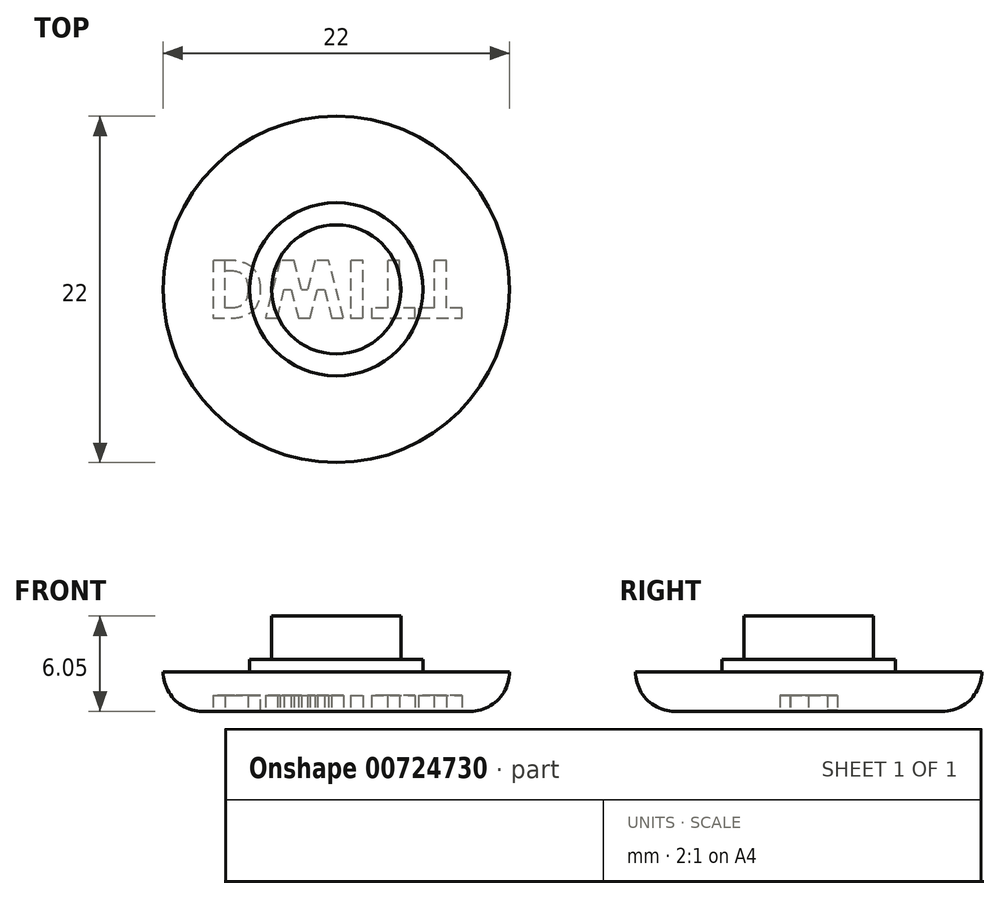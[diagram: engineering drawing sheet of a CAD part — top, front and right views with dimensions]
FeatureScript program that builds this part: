
annotation { "Feature Type Name" : "Feature", "Feature Type Description" : "" }
export const myFeature = defineFeature(function(context is Context, id is Id, definition is map)
    precondition{}
    {
        {
            var Q0;
            Q0=qCreatedBy(makeId("Top.planeOp"),FACE);
            var sketch = newSketch(context, id + "F0", { "sketchPlane" : qUnion([Q0])});
            skCircle(sketch, "E0", {"center": v(0, 0) * mm, "radius": 11 * mm});
            skCircle(sketch, "E1", {"center": v(0, 0) * mm, "radius": 4.1 * mm});
            skCircle(sketch, "E2", {"center": v(0, 0) * mm, "radius": 5.5 * mm});
            skSolve(sketch);
        }
        {
            var Q0;
            Q0=makeQuery(id+"F0.imprint","IMPRINT",FACE,{"disambiguationData":[TD([[makeQuery(id+"F0.imprint","IMPRINT",EDGE,{"derivedFrom":sQuery(id+"F0.wireOp",EDGE,"E0")}),1.0]])]});
            extrude(context, id + "F1", {"entities" : qUnion([Q0]), "depth" : 2.5 * mm, "offsetDistance" : 25 * mm});
        }
        {
            var Q0;
            Q0=makeQuery(id+"F0.imprint","IMPRINT",FACE,{"disambiguationData":[TD([[makeQuery(id+"F0.imprint","IMPRINT",EDGE,{"derivedFrom":sQuery(id+"F0.wireOp",EDGE,"E1")}),-1.0]])]});
            var Q1;
            Q1=makeQuery(id+"F1.opExtrude","CAP_FACE",FACE,{"disambiguationData":[OSD([sQuery(id+"F0.wireOp",EDGE,"E0"),sQuery(id+"F0.wireOp",EDGE,"E2")])],"isStart":false});
            extrude(context, id + "F2", {"entities" : qUnion([Q0]), "operationType" : NewBodyOperationType.ADD, "endBound" : BoundingType.UP_TO_SURFACE, "depth" : 25 * mm, "endBoundEntityFace" : qUnion([Q1]), "hasOffset" : true, "offsetDistance" : .8 * mm, "offsetOppositeDirection" : true});
        }
        {
            var Q0;
            Q0=makeQuery(id+"F0.imprint","IMPRINT",FACE,{"disambiguationData":[TD([[makeQuery(id+"F0.imprint","IMPRINT",EDGE,{"derivedFrom":sQuery(id+"F0.wireOp",EDGE,"E1")}),1.0]])]});
            var Q1;
            Q1=makeQuery(id+"F2.opExtrude","CAP_FACE",FACE,{"disambiguationData":[OSD([sQuery(id+"F0.wireOp",EDGE,"E0"),sQuery(id+"F0.wireOp",EDGE,"E2")])],"isStart":false});
            extrude(context, id + "F3", {"entities" : qUnion([Q0]), "operationType" : NewBodyOperationType.ADD, "endBound" : BoundingType.UP_TO_SURFACE, "depth" : 3 * mm, "endBoundEntityFace" : qUnion([Q1]), "hasOffset" : true, "offsetDistance" : 2.75 * mm, "offsetOppositeDirection" : true});
        }
        {
            var Q0;
            {var subQ0=sQuery(id+"F0.wireOp",EDGE,"E1");var subQ1=sQuery(id+"F0.wireOp",EDGE,"E2");Q0=makeQuery(id+"F3.boolean.opBoolean","MERGE",FACE,{"derivedFrom":[makeQuery(id+"F2.boolean.opBoolean","MERGE",FACE,{"derivedFrom":[makeQuery(id+"F1.opExtrude","CAP_FACE",FACE,{"disambiguationData":[OSD([sQuery(id+"F0.wireOp",EDGE,"E0"),subQ1])],"isStart":true}),makeQuery(id+"F2.opExtrude","CAP_FACE",FACE,{"disambiguationData":[OSD([subQ0,subQ1])],"isStart":true})]}),makeQuery(id+"F3.opExtrude","CAP_FACE",FACE,{"disambiguationData":[OSD([subQ0])],"isStart":true})]});}
            fillet(context, id + "F4", {"entities" : qUnion([Q0]), "radius" : 2.5 * mm, "tangentPropagation" : true, "allowEdgeOverflow" : false});
        }
        {
            var Q0;
            Q0=qCreatedBy(makeId("Right.planeOp"),FACE);
            var sketch = newSketch(context, id + "F5", { "sketchPlane" : qUnion([Q0])});
            skEllipse(sketch, "E3", {"center": v(-63.43, -1.89) * mm, "majorRadius": 11 * mm, "minorRadius": 2.5 * mm, "majorAxis": v(-1, 0)});
            skPoint(sketch, "E4", {"position": v(-63.43, 0.61) * mm});
            skLineSegment(sketch, "E5", {"start": v(-55.79, 0) * mm, "end": v(-71.08, 0) * mm});
            skArc(sketch, "E6", {"start": v(-11, 2.37) * mm, "mid": v(-6, 2.57) * mm, "end": v(-11, 2.5) * mm});
            skArc(sketch, "E7", {"start": v(6, 2.5) * mm, "mid": v(6, 2.46) * mm, "end": v(6, 2.42) * mm});
            skLineSegment(sketch, "E8", {"start": v(-63.43, 0.61) * mm, "end": v(-63.43, -4.39) * mm});
            skPoint(sketch, "E9.orphan", {"position": v(-63.43, -3.78) * mm});
            skPoint(sketch, "E10.orphan", {"position": v(-63.43, 0) * mm});
            skSolve(sketch);
        }
        {
            var Q0;
            {var subQ0=sQuery(id+"F0.wireOp",EDGE,"E1");var subQ1=sQuery(id+"F0.wireOp",EDGE,"E2");Q0=makeQuery(id+"F3.boolean.opBoolean","MERGE",FACE,{"derivedFrom":[makeQuery(id+"F2.boolean.opBoolean","MERGE",FACE,{"derivedFrom":[makeQuery(id+"F1.opExtrude","CAP_FACE",FACE,{"disambiguationData":[OSD([sQuery(id+"F0.wireOp",EDGE,"E0"),subQ1])],"isStart":true}),makeQuery(id+"F2.opExtrude","CAP_FACE",FACE,{"disambiguationData":[OSD([subQ0,subQ1])],"isStart":true})]}),makeQuery(id+"F3.opExtrude","CAP_FACE",FACE,{"disambiguationData":[OSD([subQ0])],"isStart":true})]});}
            var sketch = newSketch(context, id + "F6", { "sketchPlane" : qUnion([Q0])});
            skSolve(sketch);
        }
        {
            var Q0;
            {var subQ0=sQuery(id+"F0.wireOp",EDGE,"E1");var subQ1=sQuery(id+"F0.wireOp",EDGE,"E2");var subQ2=sQuery(id+"F0.wireOp",EDGE,"E0");Q0=makeQuery(id+"F6.imprint","IMPRINT",FACE,{"disambiguationData":[TD([[makeQuery(id+"F6.imprint","IMPRINT",EDGE,{"derivedFrom":makeQuery(id+"F4.opFillet","BLEND_EDGE",EDGE,{"blendedFrom":[makeQuery(id+"F1.opExtrude","CAP_EDGE",EDGE,{"disambiguationData":[OSD([subQ2])],"isStart":true}),makeQuery(id+"F3.boolean.opBoolean","MERGE",FACE,{"derivedFrom":[makeQuery(id+"F2.boolean.opBoolean","MERGE",FACE,{"derivedFrom":[makeQuery(id+"F1.opExtrude","CAP_FACE",FACE,{"disambiguationData":[OSD([subQ2,subQ1])],"isStart":true}),makeQuery(id+"F2.opExtrude","CAP_FACE",FACE,{"disambiguationData":[OSD([subQ0,subQ1])],"isStart":true})]}),makeQuery(id+"F3.opExtrude","CAP_FACE",FACE,{"disambiguationData":[OSD([subQ0])],"isStart":true})]})],"blendedInto":[makeQuery(id+"F3.boolean.opBoolean","MERGE",FACE,{"derivedFrom":[makeQuery(id+"F2.boolean.opBoolean","MERGE",FACE,{"derivedFrom":[makeQuery(id+"F1.opExtrude","CAP_FACE",FACE,{"disambiguationData":[OSD([subQ2,subQ1])],"isStart":true}),makeQuery(id+"F2.opExtrude","CAP_FACE",FACE,{"disambiguationData":[OSD([subQ0,subQ1])],"isStart":true})]}),makeQuery(id+"F3.opExtrude","CAP_FACE",FACE,{"disambiguationData":[OSD([subQ0])],"isStart":true})]})]})}),1.0]])]});}
            var sketch = newSketch(context, id + "F7", { "sketchPlane" : qUnion([Q0])});
            skLineSegment(sketch, "E11", {"start": v(-8.5, 0) * mm, "end": v(8.5, 0) * mm});
            skText(sketch, "E12", { "text": "DWITT", "fontName": "OpenSans-Bold.ttf"});
            const initialGuessF7  = {"E12": [-0.0083, -0.00184, 1, 0, 0.00369]};
            skSetInitialGuess(sketch, initialGuessF7);
            skSolve(sketch);
        }
        {
            var Q0;
            Q0 = qSketchRegion(id + "F7", true);
            extrude(context, id + "F8", {"entities" : qUnion([Q0]), "operationType" : NewBodyOperationType.REMOVE, "oppositeDirection" : true, "depth" : 1 * mm, "offsetDistance" : 25 * mm});
        }
        {
            var Q0;
            {var subQ3=sQuery(id+"F0.wireOp",EDGE,"E0");var subQ8=sQuery(id+"F0.wireOp",EDGE,"E1");var subQ9=sQuery(id+"F0.wireOp",EDGE,"E2");Q0=makeQuery(id+"F8.boolean.opBoolean","SPLIT",FACE,{"disambiguationData":[TD([makeQuery(id+"F4.opFillet","BLEND_FACE",FACE,{"disambiguationData":[OSD([subQ3])]})])],"derivedFrom":makeQuery(id+"F3.boolean.opBoolean","MERGE",FACE,{"derivedFrom":[makeQuery(id+"F2.boolean.opBoolean","MERGE",FACE,{"derivedFrom":[makeQuery(id+"F1.opExtrude","CAP_FACE",FACE,{"disambiguationData":[OSD([subQ3,subQ9])],"isStart":true}),makeQuery(id+"F2.opExtrude","CAP_FACE",FACE,{"disambiguationData":[OSD([subQ8,subQ9])],"isStart":true})]}),makeQuery(id+"F3.opExtrude","CAP_FACE",FACE,{"disambiguationData":[OSD([subQ8])],"isStart":true})]})});}
            var sketch = newSketch(context, id + "F9", { "sketchPlane" : qUnion([Q0])});
            skLineSegment(sketch, "E13.bottom", {"start": v(-7.06, -1.2) * mm, "end": v(-7.06, -1.2) * mm});
            skLineSegment(sketch, "E13.top", {"start": v(-7.06, -1.84) * mm, "end": v(-7.06, -1.84) * mm});
            skLineSegment(sketch, "E13.left", {"start": v(-7.06, -1.2) * mm, "end": v(-7.06, -1.84) * mm});
            skLineSegment(sketch, "E13.right", {"start": v(-7.06, -1.2) * mm, "end": v(-7.06, -1.84) * mm});
            skSolve(sketch);
        }
        {
            var Q0;
            Q0 = qSketchRegion(id + "F9", true);
            extrude(context, id + "F10", {"entities" : qUnion([Q0]), "operationType" : NewBodyOperationType.ADD, "oppositeDirection" : true, "depth" : .1 * mm, "offsetDistance" : 25 * mm});
        }
    });
